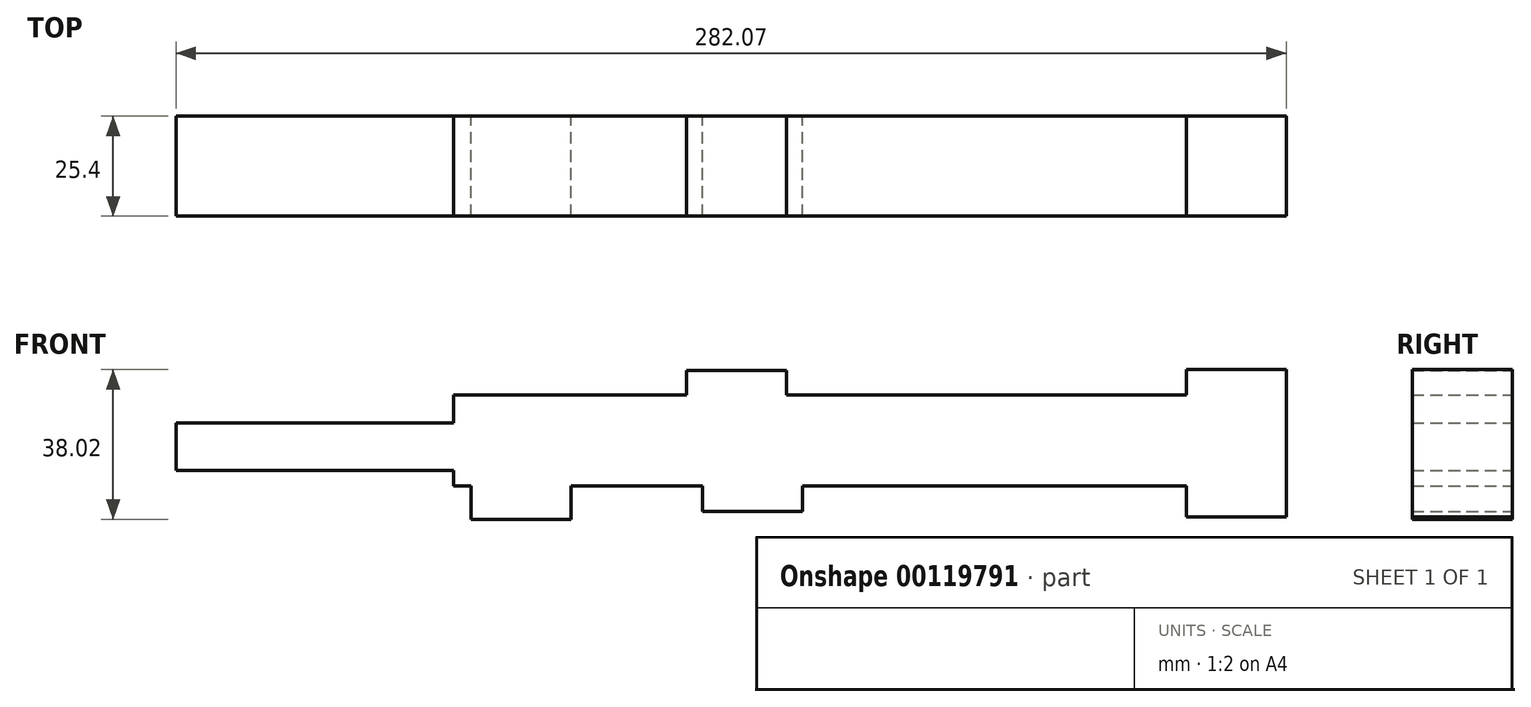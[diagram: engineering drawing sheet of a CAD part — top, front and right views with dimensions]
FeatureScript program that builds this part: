
annotation { "Feature Type Name" : "Feature", "Feature Type Description" : "" }
export const myFeature = defineFeature(function(context is Context, id is Id, definition is map)
    precondition{}
    {
        {
            var Q0;
            Q0=qCreatedBy(makeId("Front.planeOp"),FACE);
            var sketch = newSketch(context, id + "F0", { "sketchPlane" : qUnion([Q0])});
            skLineSegment(sketch, "E0.bottom", {"start": v(-59.15, 34.3) * mm, "end": v(84.92, 34.3) * mm});
            skLineSegment(sketch, "E0.top", {"start": v(-59.15, 11.17) * mm, "end": v(84.92, 11.17) * mm});
            skLineSegment(sketch, "E0.left", {"start": v(-59.15, 34.3) * mm, "end": v(-59.15, 11.17) * mm});
            skLineSegment(sketch, "E0.right", {"start": v(84.92, 34.3) * mm, "end": v(84.92, 11.17) * mm});
            skLineSegment(sketch, "E1", {"start": v(-59.15, 27.08) * mm, "end": v(-129.67, 27.08) * mm});
            skLineSegment(sketch, "E2", {"start": v(-129.67, 27.08) * mm, "end": v(-129.67, 22.23) * mm});
            skLineSegment(sketch, "E3", {"start": v(-129.67, 22.23) * mm, "end": v(-129.67, 15.06) * mm});
            skLineSegment(sketch, "E4", {"start": v(-129.67, 15.06) * mm, "end": v(-59.15, 15.06) * mm});
            skLineSegment(sketch, "E5", {"start": v(-59.15, 15.06) * mm, "end": v(-59.15, 11.17) * mm});
            skLineSegment(sketch, "E6", {"start": v(-127, 34.3) * mm, "end": v(-127, 41.25) * mm});
            skLineSegment(sketch, "E7", {"start": v(-127, 41.25) * mm, "end": v(-101.6, 41.25) * mm});
            skLineSegment(sketch, "E8", {"start": v(-101.6, 41.25) * mm, "end": v(-101.6, 34.3) * mm});
            skLineSegment(sketch, "E9", {"start": v(-101.6, 34.3) * mm, "end": v(0, 34.3) * mm});
            skLineSegment(sketch, "E10", {"start": v(0, 34.3) * mm, "end": v(0, 40.44) * mm});
            skLineSegment(sketch, "E11", {"start": v(0, 40.44) * mm, "end": v(25.4, 40.44) * mm});
            skLineSegment(sketch, "E12", {"start": v(25.4, 40.44) * mm, "end": v(25.4, 34.3) * mm});
            skLineSegment(sketch, "E13", {"start": v(25.4, 34.3) * mm, "end": v(127, 34.3) * mm});
            skLineSegment(sketch, "E14", {"start": v(127, 34.3) * mm, "end": v(127, 40.68) * mm});
            skLineSegment(sketch, "E15", {"start": v(127, 40.68) * mm, "end": v(152.4, 40.68) * mm});
            skLineSegment(sketch, "E16", {"start": v(152.4, 40.68) * mm, "end": v(152.4, 34.3) * mm});
            skLineSegment(sketch, "E17", {"start": v(152.4, 34.3) * mm, "end": v(152.4, 11.17) * mm});
            skLineSegment(sketch, "E18", {"start": v(152.4, 11.17) * mm, "end": v(152.4, 3.3) * mm});
            skLineSegment(sketch, "E19", {"start": v(152.4, 3.3) * mm, "end": v(127, 3.3) * mm});
            skLineSegment(sketch, "E20", {"start": v(127, 3.3) * mm, "end": v(127, 11.17) * mm});
            skLineSegment(sketch, "E21", {"start": v(127, 11.17) * mm, "end": v(29.44, 11.17) * mm});
            skLineSegment(sketch, "E22", {"start": v(29.44, 11.17) * mm, "end": v(29.44, 4.61) * mm});
            skLineSegment(sketch, "E23", {"start": v(29.44, 4.61) * mm, "end": v(4.04, 4.61) * mm});
            skLineSegment(sketch, "E24", {"start": v(4.04, 4.61) * mm, "end": v(4.04, 11.17) * mm});
            skLineSegment(sketch, "E25", {"start": v(4.04, 11.17) * mm, "end": v(-29.26, 11.17) * mm});
            skLineSegment(sketch, "E26", {"start": v(-29.26, 11.17) * mm, "end": v(-29.26, 2.66) * mm});
            skLineSegment(sketch, "E27", {"start": v(-29.26, 2.66) * mm, "end": v(-54.66, 2.66) * mm});
            skLineSegment(sketch, "E28", {"start": v(-54.66, 2.66) * mm, "end": v(-54.66, 11.17) * mm});
            skSolve(sketch);
        }
        {
            var Q0;
            Q0 = qSketchRegion(id + "F0", true);
            var Q1;
            Q1=sQuery(id+"F0.wireOp",EDGE,"E4");
            var Q2;
            Q2=sQuery(id+"F0.wireOp",EDGE,"E7");
            var Q3;
            Q3=sQuery(id+"F0.wireOp",EDGE,"E9");
            var Q4;
            Q4=sQuery(id+"F0.wireOp",EDGE,"E0.right");
            var Q5;
            Q5=sQuery(id+"F0.wireOp",EDGE,"E0.left");
            var Q6;
            Q6=sQuery(id+"F0.wireOp",EDGE,"E0.top");
            var Q7;
            Q7=sQuery(id+"F0.wireOp",EDGE,"E0.bottom");
            var Q8;
            Q8=sQuery(id+"F0.wireOp",EDGE,"E17");
            var Q9;
            Q9=sQuery(id+"F0.wireOp",EDGE,"E27");
            var Q10;
            Q10=sQuery(id+"F0.wireOp",EDGE,"E19");
            var Q11;
            Q11=sQuery(id+"F0.wireOp",EDGE,"E13");
            var Q12;
            Q12=sQuery(id+"F0.wireOp",EDGE,"E21");
            var Q13;
            Q13=sQuery(id+"F0.wireOp",EDGE,"E25");
            var Q14;
            Q14=sQuery(id+"F0.wireOp",EDGE,"E15");
            var Q15;
            Q15=sQuery(id+"F0.wireOp",EDGE,"E11");
            var Q16;
            Q16=sQuery(id+"F0.wireOp",EDGE,"E23");
            var Q17;
            Q17=sQuery(id+"F0.wireOp",EDGE,"E6");
            var Q18;
            Q18=sQuery(id+"F0.wireOp",EDGE,"E28");
            var Q19;
            Q19=sQuery(id+"F0.wireOp",EDGE,"E3");
            var Q20;
            Q20=sQuery(id+"F0.wireOp",EDGE,"E8");
            var Q21;
            Q21=sQuery(id+"F0.wireOp",EDGE,"E24");
            var Q22;
            Q22=sQuery(id+"F0.wireOp",EDGE,"E20");
            var Q23;
            Q23=sQuery(id+"F0.wireOp",EDGE,"E14");
            var Q24;
            Q24=sQuery(id+"F0.wireOp",EDGE,"E26");
            var Q25;
            Q25=sQuery(id+"F0.wireOp",EDGE,"E12");
            var Q26;
            Q26=sQuery(id+"F0.wireOp",EDGE,"E18");
            var Q27;
            Q27=sQuery(id+"F0.wireOp",EDGE,"E22");
            var Q28;
            Q28=sQuery(id+"F0.wireOp",EDGE,"E10");
            var Q29;
            Q29=sQuery(id+"F0.wireOp",EDGE,"E16");
            var Q30;
            Q30=sQuery(id+"F0.wireOp",EDGE,"E5");
            var Q31;
            Q31=sQuery(id+"F0.wireOp",EDGE,"E1");
            var Q32;
            Q32=sQuery(id+"F0.wireOp",EDGE,"E2");
            extrude(context, id + "F1", {"entities" : qUnion([Q0]), "surfaceEntities" : qUnion([Q1, Q2, Q3, Q4, Q5, Q6, Q7, Q8, Q9, Q10, Q11, Q12, Q13, Q14, Q15, Q16, Q17, Q18, Q19, Q20, Q21, Q22, Q23, Q24, Q25, Q26, Q27, Q28, Q29, Q30, Q31, Q32]), "depth" : 25.4 * mm});
        }
    });
